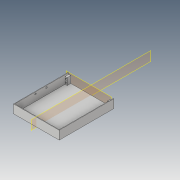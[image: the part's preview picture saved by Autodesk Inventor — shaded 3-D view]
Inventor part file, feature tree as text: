
AUTODESK INVENTOR PART (.ipt)
format: ipt  version: 2019 (Build 230136000, 136)  size: 250,880 bytes
history: native  units: mm
features: sketch x11, extrude x7, hole x4, plane x2, mirror x1, projected_geometry x1
ambient origin geometry x8: Origin, YZ Plane, XZ Plane, XY Plane, X Axis, Y Axis, Z Axis, Center Point
bodies: Solid1 (feature_tree)
feature tree (26):
  sketch  "Sketch1"  dims[d0=295.0mm d1=105.0mm]
  sketch  "Sketch2"  dims[d2=7.6mm d3=3.0mm]
  extrude  "Extrusion1"  Depth=105.0mm
  extrude  "Extrusion2"  Depth=3.0mm
  extrude  "Extrusion4"  Depth=1.0mm TaperAngle=0.0deg
  extrude  "Extrusion6"  Depth=1.0mm
  plane  "Work Plane2"
  plane  "Work Plane4"
  hole  "Hole3"  [1 undecoded]
  hole  "Hole4"  [1 undecoded]
  hole  "Hole5"  [1 undecoded]
  hole  "Hole6"  [1 undecoded]
  mirror  "Mirror6"
  extrude  "Extrusion14"  TaperAngle=150.0deg  [1 undecoded]
  extrude  "Extrusion15"  Depth=4.0mm
  extrude  "Extrusion16"  Depth=4.0mm
  sketch  "Sketch5"  dims[d4=14.0mm d7=1.0mm d8=0.0mm]
  sketch  "Sketch7"  dims[d9=23.0mm d10=1.0mm d11=0.0mm d12=0.0mm d35=4.5mm]
  projected_geometry  "Projected Loop4"
  sketch  "Sketch16"  dims[d37=4.5mm d39=4.5mm]
  sketch  "Sketch17"  dims[d40=0.0mm d41=30.8mm]
  sketch  "Sketch18"  dims[d45=4.5mm d46=0.0mm]
  sketch  "Sketch19"  dims[d47=30.8mm d50=10.0mm d51=0.0mm]
  sketch  "Sketch23"  dims[d57=135.0deg d58=135.0deg d61=6.0mm d62=0.0mm d64=150.0deg d65=150.0deg]
  sketch  "Sketch24"  dims[d71=10.0mm d72=4.0mm]
  sketch  "Sketch25"  dims[d73=10.0mm d74=4.0mm d75=1.5mm d76=60.0mm d77=60.0mm d106=10.0mm d107=10.0mm d108=3.5mm d110=2.6mm d111=6.0mm d112=5.0mm d113=2.0mm d114=14.3117mm d115=5.0mm d116=0.0mm d117=2.6mm d118=6.0mm d119=5.0mm d120=2.0mm d121=14.3117mm d122=15.0mm d123=20.594885mm d124=3.5mm d125=5.0mm d126=2.6mm d127=6.0mm d128=5.0mm d129=2.0mm d130=14.3117mm d131=5.0mm d132=0.0mm d133=2.6mm d134=6.0mm d135=5.0mm d136=2.0mm d137=14.3117mm d138=15.0mm d139=20.594885mm d144=5.0mm d145=5.0mm d148=151.5mm d149=151.5mm d159=4.0mm d160=4.0mm d161=2.2mm d162=2.0mm d163=2.0mm d164=4.0mm d165=4.0mm d166=2.2mm d167=2.0mm d168=2.0mm d169=4.0mm d170=4.0mm d171=2.2mm d172=2.0mm d173=2.0mm d174=4.0mm d175=4.0mm d176=2.2mm d177=2.0mm d178=2.0mm d179=19.0mm d180=0.0mm d181=9.0mm d182=5.0mm d183=4.0mm d184=30.0mm d185=20.0mm d186=0.0mm d187=9.0mm d188=5.0mm d189=40.0mm d190=4.0mm d191=20.0mm d192=0.0mm d193=19.0mm d194=5.0mm d91=1.0mm d92=1.0mm d93=1.0mm d94=0.15mm d95=0.25mm d96=0.375mm d97=14.3117mm d98=0.75mm d99=20.594885mm d100=0.0625mm d101=0.75mm d102=0.375mm]
note: 5 required parameter values undecoded (feature->parameter linkage not recoverable at this tier; creation-order binding heuristic only, values carry confidence <= 0.55)
